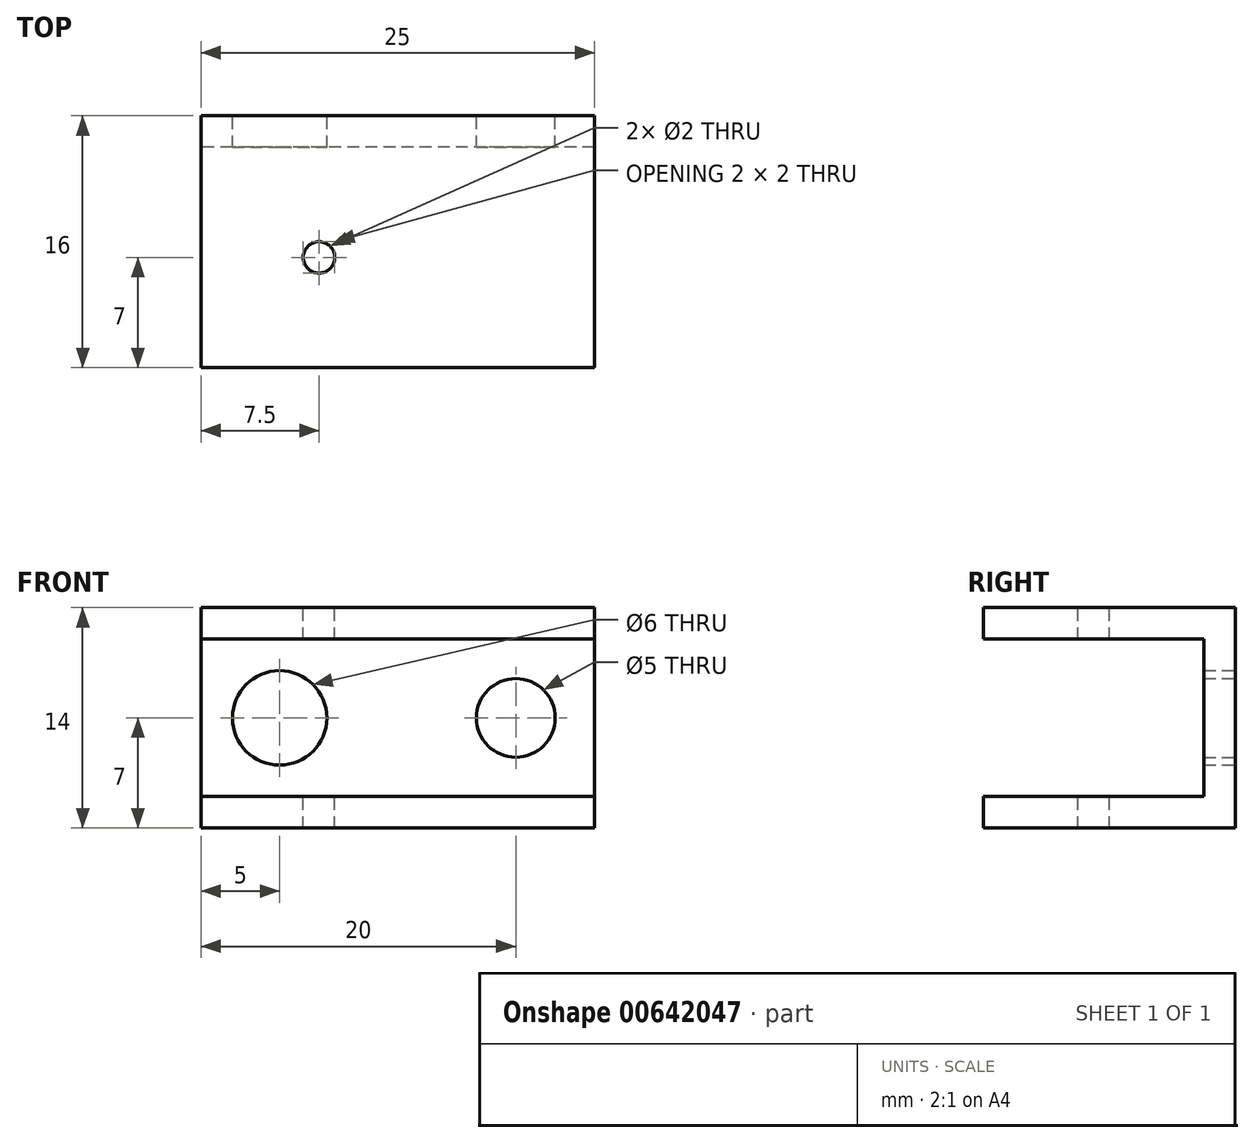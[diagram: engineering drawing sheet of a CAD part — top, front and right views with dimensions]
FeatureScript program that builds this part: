
annotation { "Feature Type Name" : "Feature", "Feature Type Description" : "" }
export const myFeature = defineFeature(function(context is Context, id is Id, definition is map)
    precondition{}
    {
        {
            var Q0;
            Q0=qCreatedBy(makeId("Front.planeOp"),FACE);
            var sketch = newSketch(context, id + "F0", { "sketchPlane" : qUnion([Q0])});
            skLineSegment(sketch, "E0.bottom", {"start": v(-12.5, 7) * mm, "end": v(12.5, 7) * mm});
            skLineSegment(sketch, "E0.top", {"start": v(-12.5, -7) * mm, "end": v(12.5, -7) * mm});
            skLineSegment(sketch, "E0.left", {"start": v(-12.5, 7) * mm, "end": v(-12.5, -7) * mm});
            skLineSegment(sketch, "E0.right", {"start": v(12.5, 7) * mm, "end": v(12.5, -7) * mm});
            skCircle(sketch, "E1", {"center": v(-7.5, 0) * mm, "radius": 3 * mm});
            skCircle(sketch, "E2", {"center": v(7.5, 0) * mm, "radius": 2.5 * mm});
            skSolve(sketch);
        }
        {
            var Q0;
            Q0=makeQuery(id+"F0.imprint","IMPRINT",FACE,{"disambiguationData":[TD([[makeQuery(id+"F0.imprint","IMPRINT",EDGE,{"derivedFrom":sQuery(id+"F0.wireOp",EDGE,"E0.bottom")}),-1.0]])]});
            extrude(context, id + "F1", {"entities" : qUnion([Q0]), "depth" : 16 * mm, "offsetDistance" : 25 * mm});
        }
        {
            var Q0;
            Q0=makeQuery(id+"F1.opExtrude","SWEPT_FACE",FACE,{"disambiguationData":[OSD([sQuery(id+"F0.wireOp",EDGE,"E0.bottom")])]});
            var sketch = newSketch(context, id + "F2", { "sketchPlane" : qUnion([Q0])});
            skCircle(sketch, "E3", {"center": v(-5, -9) * mm, "radius": 1 * mm});
            skSolve(sketch);
        }
        {
            var Q0;
            Q0=makeQuery(id+"F2.imprint","IMPRINT",FACE,{"disambiguationData":[TD([[makeQuery(id+"F2.imprint","IMPRINT",EDGE,{"derivedFrom":sQuery(id+"F2.wireOp",EDGE,"E3")}),1.0]])]});
            var Q1;
            Q1=sQuery(id+"F2.wireOp",EDGE,"E3");
            extrude(context, id + "F3", {"entities" : qUnion([Q0]), "operationType" : NewBodyOperationType.REMOVE, "surfaceEntities" : qUnion([Q1]), "oppositeDirection" : true, "depth" : 25 * mm, "offsetDistance" : 25 * mm});
        }
        {
            var Q0;
            Q0=makeQuery(id+"F1.opExtrude","SWEPT_FACE",FACE,{"disambiguationData":[OSD([sQuery(id+"F0.wireOp",EDGE,"E0.left")])]});
            var sketch = newSketch(context, id + "F4", { "sketchPlane" : qUnion([Q0])});
            skLineSegment(sketch, "E4.bottom", {"start": v(2, 5) * mm, "end": v(16, 5) * mm});
            skLineSegment(sketch, "E4.top", {"start": v(2, -5) * mm, "end": v(16, -5) * mm});
            skLineSegment(sketch, "E4.left", {"start": v(2, 5) * mm, "end": v(2, -5) * mm});
            skLineSegment(sketch, "E4.right", {"start": v(16, 5) * mm, "end": v(16, -5) * mm});
            skSolve(sketch);
        }
        {
            var Q0;
            Q0=makeQuery(id+"F4.imprint","IMPRINT",FACE,{"disambiguationData":[TD([[makeQuery(id+"F4.imprint","IMPRINT",EDGE,{"derivedFrom":sQuery(id+"F4.wireOp",EDGE,"E4.bottom")}),-1.0]])]});
            extrude(context, id + "F5", {"entities" : qUnion([Q0]), "operationType" : NewBodyOperationType.REMOVE, "oppositeDirection" : true, "depth" : 25 * mm, "offsetDistance" : 25 * mm});
        }
    });
